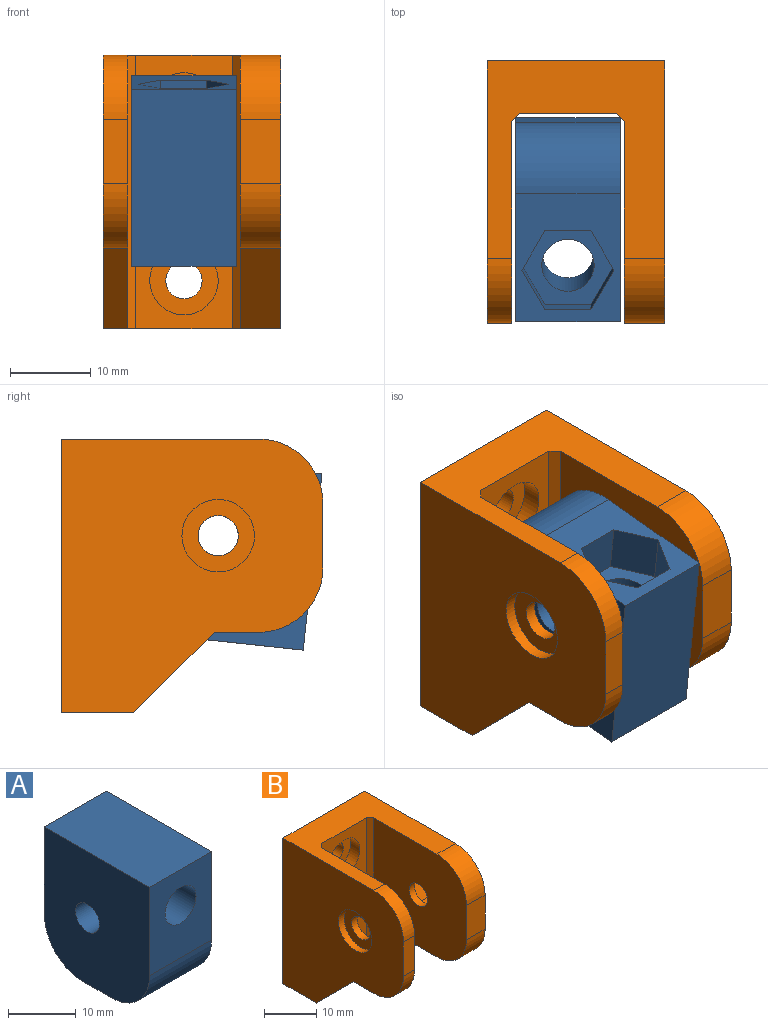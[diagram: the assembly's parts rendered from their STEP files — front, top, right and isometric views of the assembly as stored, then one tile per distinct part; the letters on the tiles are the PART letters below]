
ASSEMBLY  parts=2 mates=1
PART A: 17 faces, bbox 13x22x24 mm
  f0: plane 16x13mm, normal (0,-1,0), area 174.8mm2, adj f1,f5,f6,f8,f16
  f1: plane 22x13mm, normal (0,0,1), area 286mm2, adj f0,f2,f5,f6
  f2: plane 16x13mm, normal (0,1,0), area 123.1mm2, adj f1,f5,f6,f7,f9,f10,f11,f12
  f3: plane 13x6mm, normal (0,0,-1), area 78mm2, adj f5,f6,f7,f8
  f4: cylinder r=2.5mm len=13mm, axis (1,0,0), area 200.6mm2, adj f5,f6,f16
  f5: plane 24x22mm, normal (-1,0,0), area 480.9mm2, adj f0,f1,f2,f3,f4,f7,f8
  f6: plane 24x22mm, normal (1,0,0), area 480.9mm2, adj f0,f1,f2,f3,f4,f7,f8
  f7: cylinder r=8mm len=13mm, axis (-1,0,0), area 163.4mm2, adj f2,f3,f5,f6
  f8: cylinder r=8mm len=13mm, axis (1,0,0), area 163.4mm2, adj f0,f3,f5,f6
  f9: plane 5.9x4.95mm, normal (0.87,0,-0.5), area 33.7mm2, adj f2,f10,f14,f15
  f10: plane 5.9x5.72mm, normal (0,0,-1), area 33.7mm2, adj f2,f9,f11,f15
  f11: plane 5.9x4.95mm, normal (-0.87,0,-0.5), area 33.7mm2, adj f2,f10,f12,f15
  f12: plane 5.9x4.95mm, normal (-0.87,0,0.5), area 33.7mm2, adj f2,f11,f13,f15
  f13: plane 5.9x5.72mm, normal (0,0,1), area 33.7mm2, adj f2,f12,f14,f15
  f14: plane 5.9x4.95mm, normal (0.87,0,0.5), area 33.7mm2, adj f2,f9,f13,f15
  f15: plane 11.43x9.9mm, normal (0,1,0), area 51.7mm2, adj f9,f10,f11,f12,f13,f14,f16
  f16: cylinder r=3.25mm len=16.1mm, axis (0,1,0), area 325.2mm2, adj f0,f4,f15
PART B: 37 faces, bbox 22x32.5x34 mm
  f0: plane 34x25mm, normal (1,0,0), area 617.9mm2, adj f2,f3,f7,f8,f12,f19,f20,f33
  f1: plane 34x12mm, normal (0,-1,0), area 294.5mm2, adj f7,f8,f15,f18,f34,f35
  f2: plane 5.5x3mm, normal (0,0,-1), area 16.5mm2, adj f0,f6,f19,f33
  f3: cylinder r=2.5mm len=5mm, axis (-1,0,0), area 23.6mm2, adj f0,f32
  f4: plane 5.5x5mm, normal (0,0,-1), area 27.5mm2, adj f10,f21,f30,f36
  f5: cylinder r=2.5mm len=5mm, axis (-1,0,0), area 23.6mm2, adj f10,f29
  f6: plane 34x32.5mm, normal (-1,0,0), area 828.9mm2, adj f2,f7,f8,f9,f12,f19,f20,f31
  f7: plane 22x9mm, normal (0,0,-1), area 164mm2, adj f0,f1,f6,f9,f10,f30,f33,f34
  f8: plane 24.5x22mm, normal (0,0,1), area 288mm2, adj f0,f1,f6,f9,f10,f20,f22,f34
  f9: plane 34x22mm, normal (0,1,0), area 716.2mm2, adj f6,f7,f8,f13,f16,f36
  f10: plane 34x25mm, normal (-1,0,0), area 617.9mm2, adj f4,f5,f7,f8,f11,f21,f22,f30
  f11: plane 8x5mm, normal (0,-1,0), area 40mm2, adj f10,f21,f22,f36
  f12: plane 8x3mm, normal (0,-1,0), area 24mm2, adj f0,f6,f19,f20
  f13: cylinder r=2.25mm len=4.5mm, axis (0,-1,0), area 56.5mm2, adj f9,f14
  f14: plane 8.5x8.5mm, normal (0,-1,0), area 40.8mm2, adj f13,f15
  f15: cylinder r=4.25mm len=8.5mm, axis (0,-1,0), area 66.8mm2, adj f1,f14
  f16: cylinder r=2.25mm len=4.5mm, axis (0,-1,0), area 56.5mm2, adj f9,f17
  f17: plane 8.5x8.5mm, normal (0,-1,0), area 40.8mm2, adj f16,f18
  f18: cylinder r=4.25mm len=8.5mm, axis (0,-1,0), area 66.8mm2, adj f1,f17
  f19: cylinder r=8mm len=8mm, axis (-1,0,0), area 37.7mm2, adj f0,f2,f6,f12
  f20: cylinder r=8mm len=8mm, axis (-1,0,0), area 37.7mm2, adj f0,f6,f8,f12
  f21: cylinder r=8mm len=8mm, axis (-1,0,0), area 62.8mm2, adj f4,f10,f11,f36
  f22: cylinder r=8mm len=8mm, axis (-1,0,0), area 62.8mm2, adj f8,f10,f11,f36
  f23: plane 4.3x3.5mm, normal (0,-0.87,-0.5), area 17.4mm2, adj f24,f28,f29,f36
  f24: plane 4.97x3.5mm, normal (0,0,-1), area 17.4mm2, adj f23,f25,f29,f36
  f25: plane 4.3x3.5mm, normal (0,0.87,-0.5), area 17.4mm2, adj f24,f26,f29,f36
  f26: plane 4.3x3.5mm, normal (0,0.87,0.5), area 17.4mm2, adj f25,f27,f29,f36
  f27: plane 4.97x3.5mm, normal (0,0,1), area 17.4mm2, adj f26,f28,f29,f36
  f28: plane 4.3x3.5mm, normal (0,-0.87,0.5), area 17.4mm2, adj f23,f27,f29,f36
  f29: plane 9.93x8.6mm, normal (1,0,0), area 44.4mm2, adj f5,f23,f24,f25,f26,f27,f28
  f30: plane 10x10mm, normal (0,-0.71,-0.71), area 70.7mm2, adj f4,f7,f10,f36
  f31: cylinder r=4.5mm len=9mm, axis (-1,0,0), area 42.4mm2, adj f6,f32
  f32: plane 9x9mm, normal (-1,0,0), area 44mm2, adj f3,f31
  f33: plane 10x10mm, normal (0,-0.71,-0.71), area 42.4mm2, adj f0,f2,f6,f7
  f34: plane 34x1mm, normal (-0.71,-0.71,0), area 48.1mm2, adj f1,f7,f8,f10
  f35: plane 34x1mm, normal (0.71,-0.71,0), area 48.1mm2, adj f0,f1,f7,f8
  f36: plane 34x32.5mm, normal (1,0,0), area 828.5mm2, adj f4,f7,f8,f9,f11,f21,f22,f23
PLACE A rot(axis=(1,0,0),96.1deg) t=(0,0.99,37.26)mm
PLACE B t=(0,-6.5,0)mm
MATE revolute B.f31 <-> A.f4  axis (-1,0,0) through (17,-19.5,22)mm
